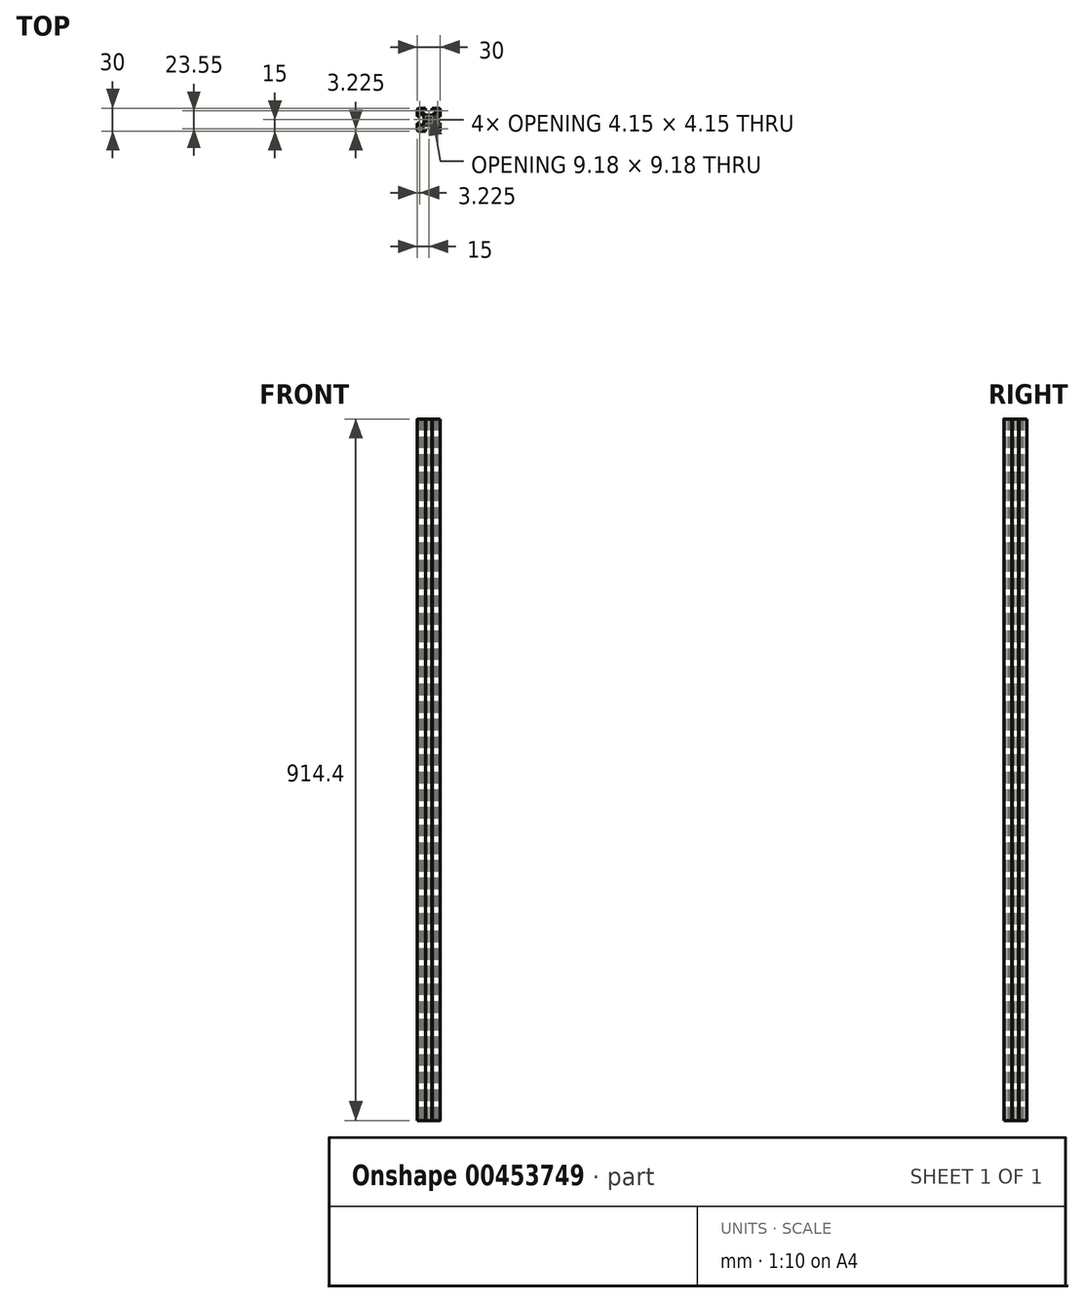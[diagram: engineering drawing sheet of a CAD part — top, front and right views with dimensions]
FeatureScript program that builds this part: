
annotation { "Feature Type Name" : "Feature", "Feature Type Description" : "" }
export const myFeature = defineFeature(function(context is Context, id is Id, definition is map)
    precondition{}
    {
        {
            var Q0;
            Q0=qCreatedBy(makeId("Top.planeOp"),FACE);
            var sketch = newSketch(context, id + "F0", { "sketchPlane" : qUnion([Q0])});
            skLineSegment(sketch, "E0", {"start": v(-12.8, -8.25) * mm, "end": v(-12.8, -4.05) * mm});
            skLineSegment(sketch, "E1", {"start": v(12.8, 4.05) * mm, "end": v(12.8, 8.25) * mm});
            skLineSegment(sketch, "E2", {"start": v(4.6, -3.19) * mm, "end": v(3.27, -1.62) * mm});
            skLineSegment(sketch, "E3", {"start": v(-3.27, 1.62) * mm, "end": v(-4.6, 3.19) * mm});
            skLineSegment(sketch, "E4", {"start": v(8.25, -10.05) * mm, "end": v(4.2, -6) * mm});
            skLineSegment(sketch, "E5", {"start": v(10.05, -8.25) * mm, "end": v(6, -4.2) * mm});
            skLineSegment(sketch, "E6", {"start": v(-3.19, -4.6) * mm, "end": v(-4.6, -3.19) * mm});
            skLineSegment(sketch, "E7", {"start": v(4.6, 3.19) * mm, "end": v(3.19, 4.6) * mm});
            skLineSegment(sketch, "E8", {"start": v(-6, 4.2) * mm, "end": v(-10.05, 8.25) * mm});
            skLineSegment(sketch, "E9", {"start": v(-4.2, 6) * mm, "end": v(-8.25, 10.05) * mm});
            skLineSegment(sketch, "E10", {"start": v(3.19, -4.6) * mm, "end": v(1.62, -3.27) * mm});
            skLineSegment(sketch, "E11", {"start": v(-1.62, 3.27) * mm, "end": v(-3.19, 4.6) * mm});
            skLineSegment(sketch, "E12", {"start": v(-4.05, -12.8) * mm, "end": v(-8.25, -12.8) * mm});
            skLineSegment(sketch, "E13", {"start": v(8.25, 12.8) * mm, "end": v(4.05, 12.8) * mm});
            skLineSegment(sketch, "E14", {"start": v(4.55, -15) * mm, "end": v(13, -15) * mm});
            skLineSegment(sketch, "E15", {"start": v(-13, -15) * mm, "end": v(-4.55, -15) * mm});
            skLineSegment(sketch, "E16", {"start": v(4.05, -14.5) * mm, "end": v(4.55, -14.5) * mm});
            skLineSegment(sketch, "E17", {"start": v(-4.55, -14.5) * mm, "end": v(-4.05, -14.5) * mm});
            skLineSegment(sketch, "E18", {"start": v(9.7, -13.85) * mm, "end": v(12.85, -13.85) * mm});
            skLineSegment(sketch, "E19", {"start": v(-12.85, -13.85) * mm, "end": v(-9.7, -13.85) * mm});
            skLineSegment(sketch, "E20", {"start": v(9.7, -9.7) * mm, "end": v(13.85, -9.7) * mm});
            skLineSegment(sketch, "E21", {"start": v(-13.85, -9.7) * mm, "end": v(-9.7, -9.7) * mm});
            skLineSegment(sketch, "E22", {"start": v(10.05, -8.25) * mm, "end": v(12.8, -8.25) * mm});
            skLineSegment(sketch, "E23", {"start": v(-12.8, -8.25) * mm, "end": v(-10.05, -8.25) * mm});
            skLineSegment(sketch, "E24", {"start": v(-4.2, -6) * mm, "end": v(4.2, -6) * mm});
            skLineSegment(sketch, "E25", {"start": v(14.5, -4.55) * mm, "end": v(15, -4.55) * mm});
            skLineSegment(sketch, "E26", {"start": v(-15, -4.55) * mm, "end": v(-14.5, -4.55) * mm});
            skLineSegment(sketch, "E27", {"start": v(12.8, -4.05) * mm, "end": v(14.5, -4.05) * mm});
            skLineSegment(sketch, "E28", {"start": v(-14.5, -4.05) * mm, "end": v(-12.8, -4.05) * mm});
            skLineSegment(sketch, "E29", {"start": v(-14.5, 4.05) * mm, "end": v(-12.8, 4.05) * mm});
            skLineSegment(sketch, "E30", {"start": v(12.8, 4.05) * mm, "end": v(14.5, 4.05) * mm});
            skLineSegment(sketch, "E31", {"start": v(-15, 4.55) * mm, "end": v(-14.5, 4.55) * mm});
            skLineSegment(sketch, "E32", {"start": v(14.5, 4.55) * mm, "end": v(15, 4.55) * mm});
            skLineSegment(sketch, "E33", {"start": v(-4.2, 6) * mm, "end": v(4.2, 6) * mm});
            skLineSegment(sketch, "E34", {"start": v(-12.8, 8.25) * mm, "end": v(-10.05, 8.25) * mm});
            skLineSegment(sketch, "E35", {"start": v(10.05, 8.25) * mm, "end": v(12.8, 8.25) * mm});
            skLineSegment(sketch, "E36", {"start": v(9.7, 9.7) * mm, "end": v(13.85, 9.7) * mm});
            skLineSegment(sketch, "E37", {"start": v(-13.85, 9.7) * mm, "end": v(-9.7, 9.7) * mm});
            skLineSegment(sketch, "E38", {"start": v(9.7, 13.85) * mm, "end": v(12.85, 13.85) * mm});
            skLineSegment(sketch, "E39", {"start": v(-12.85, 13.85) * mm, "end": v(-9.7, 13.85) * mm});
            skLineSegment(sketch, "E40", {"start": v(-4.55, 14.5) * mm, "end": v(-4.05, 14.5) * mm});
            skLineSegment(sketch, "E41", {"start": v(4.05, 14.5) * mm, "end": v(4.55, 14.5) * mm});
            skLineSegment(sketch, "E42", {"start": v(-13, 15) * mm, "end": v(-4.55, 15) * mm});
            skLineSegment(sketch, "E43", {"start": v(4.55, 15) * mm, "end": v(13, 15) * mm});
            skLineSegment(sketch, "E44", {"start": v(4.05, -12.8) * mm, "end": v(8.25, -12.8) * mm});
            skLineSegment(sketch, "E45", {"start": v(-8.25, 12.8) * mm, "end": v(-4.05, 12.8) * mm});
            skLineSegment(sketch, "E46", {"start": v(-3.19, -4.6) * mm, "end": v(-1.62, -3.27) * mm});
            skLineSegment(sketch, "E47", {"start": v(1.62, 3.27) * mm, "end": v(3.19, 4.6) * mm});
            skLineSegment(sketch, "E48", {"start": v(-8.25, -10.05) * mm, "end": v(-4.2, -6) * mm});
            skLineSegment(sketch, "E49", {"start": v(-10.05, -8.25) * mm, "end": v(-6, -4.2) * mm});
            skLineSegment(sketch, "E50", {"start": v(3.19, -4.6) * mm, "end": v(4.6, -3.19) * mm});
            skLineSegment(sketch, "E51", {"start": v(-4.6, 3.19) * mm, "end": v(-3.19, 4.6) * mm});
            skLineSegment(sketch, "E52", {"start": v(6, 4.2) * mm, "end": v(10.05, 8.25) * mm});
            skLineSegment(sketch, "E53", {"start": v(4.2, 6) * mm, "end": v(8.25, 10.05) * mm});
            skLineSegment(sketch, "E54", {"start": v(-4.6, -3.19) * mm, "end": v(-3.27, -1.62) * mm});
            skLineSegment(sketch, "E55", {"start": v(3.27, 1.62) * mm, "end": v(4.6, 3.19) * mm});
            skLineSegment(sketch, "E56", {"start": v(12.8, -8.25) * mm, "end": v(12.8, -4.05) * mm});
            skLineSegment(sketch, "E57", {"start": v(-12.8, 4.05) * mm, "end": v(-12.8, 8.25) * mm});
            skLineSegment(sketch, "E58", {"start": v(-15, -13) * mm, "end": v(-15, -4.55) * mm});
            skLineSegment(sketch, "E59", {"start": v(-15, 4.55) * mm, "end": v(-15, 13) * mm});
            skLineSegment(sketch, "E60", {"start": v(-14.5, -4.55) * mm, "end": v(-14.5, -4.05) * mm});
            skLineSegment(sketch, "E61", {"start": v(-14.5, 4.05) * mm, "end": v(-14.5, 4.55) * mm});
            skLineSegment(sketch, "E62", {"start": v(-13.85, -12.85) * mm, "end": v(-13.85, -9.7) * mm});
            skLineSegment(sketch, "E63", {"start": v(-13.85, 9.7) * mm, "end": v(-13.85, 12.85) * mm});
            skLineSegment(sketch, "E64", {"start": v(-9.7, -13.85) * mm, "end": v(-9.7, -9.7) * mm});
            skLineSegment(sketch, "E65", {"start": v(-9.7, 9.7) * mm, "end": v(-9.7, 13.85) * mm});
            skLineSegment(sketch, "E66", {"start": v(-8.25, -12.8) * mm, "end": v(-8.25, -10.05) * mm});
            skLineSegment(sketch, "E67", {"start": v(-8.25, 10.05) * mm, "end": v(-8.25, 12.8) * mm});
            skLineSegment(sketch, "E68", {"start": v(-6, -4.2) * mm, "end": v(-6, 4.2) * mm});
            skLineSegment(sketch, "E69", {"start": v(-4.55, -15) * mm, "end": v(-4.55, -14.5) * mm});
            skLineSegment(sketch, "E70", {"start": v(-4.55, 14.5) * mm, "end": v(-4.55, 15) * mm});
            skLineSegment(sketch, "E71", {"start": v(-4.05, -14.5) * mm, "end": v(-4.05, -12.8) * mm});
            skLineSegment(sketch, "E72", {"start": v(-4.05, 12.8) * mm, "end": v(-4.05, 14.5) * mm});
            skLineSegment(sketch, "E73", {"start": v(4.05, -14.5) * mm, "end": v(4.05, -12.8) * mm});
            skLineSegment(sketch, "E74", {"start": v(4.05, 12.8) * mm, "end": v(4.05, 14.5) * mm});
            skLineSegment(sketch, "E75", {"start": v(4.55, -15) * mm, "end": v(4.55, -14.5) * mm});
            skLineSegment(sketch, "E76", {"start": v(4.55, 14.5) * mm, "end": v(4.55, 15) * mm});
            skLineSegment(sketch, "E77", {"start": v(6, -4.2) * mm, "end": v(6, 4.2) * mm});
            skLineSegment(sketch, "E78", {"start": v(8.25, -12.8) * mm, "end": v(8.25, -10.05) * mm});
            skLineSegment(sketch, "E79", {"start": v(8.25, 10.05) * mm, "end": v(8.25, 12.8) * mm});
            skLineSegment(sketch, "E80", {"start": v(9.7, 9.7) * mm, "end": v(9.7, 13.85) * mm});
            skLineSegment(sketch, "E81", {"start": v(9.7, -13.85) * mm, "end": v(9.7, -9.7) * mm});
            skLineSegment(sketch, "E82", {"start": v(13.85, 9.7) * mm, "end": v(13.85, 12.85) * mm});
            skLineSegment(sketch, "E83", {"start": v(13.85, -12.85) * mm, "end": v(13.85, -9.7) * mm});
            skLineSegment(sketch, "E84", {"start": v(14.5, -4.55) * mm, "end": v(14.5, -4.05) * mm});
            skLineSegment(sketch, "E85", {"start": v(14.5, 4.05) * mm, "end": v(14.5, 4.55) * mm});
            skLineSegment(sketch, "E86", {"start": v(15, -13) * mm, "end": v(15, -4.55) * mm});
            skLineSegment(sketch, "E87", {"start": v(15, 4.55) * mm, "end": v(15, 13) * mm});
            skArc(sketch, "E88", {"start": v(-15, -13) * mm, "mid": v(-14.41, -14.41) * mm, "end": v(-13, -15) * mm});
            skArc(sketch, "E89", {"start": v(-13, 15) * mm, "mid": v(-14.41, 14.41) * mm, "end": v(-15, 13) * mm});
            skArc(sketch, "E90", {"start": v(-13.85, -12.85) * mm, "mid": v(-13.56, -13.56) * mm, "end": v(-12.85, -13.85) * mm});
            skArc(sketch, "E91", {"start": v(-12.85, 13.85) * mm, "mid": v(-13.56, 13.56) * mm, "end": v(-13.85, 12.85) * mm});
            skArc(sketch, "E92", {"start": v(-1.62, -3.27) * mm, "mid": v(0, -3.65) * mm, "end": v(1.62, -3.27) * mm});
            skArc(sketch, "E93", {"start": v(-3.27, 1.62) * mm, "mid": v(-3.65, 0) * mm, "end": v(-3.27, -1.62) * mm});
            skArc(sketch, "E94", {"start": v(1.62, 3.27) * mm, "mid": v(0, 3.65) * mm, "end": v(-1.62, 3.27) * mm});
            skArc(sketch, "E95", {"start": v(3.27, -1.62) * mm, "mid": v(3.65, 0) * mm, "end": v(3.27, 1.62) * mm});
            skArc(sketch, "E96", {"start": v(12.85, -13.85) * mm, "mid": v(13.56, -13.56) * mm, "end": v(13.85, -12.85) * mm});
            skArc(sketch, "E97", {"start": v(13.85, 12.85) * mm, "mid": v(13.56, 13.56) * mm, "end": v(12.85, 13.85) * mm});
            skArc(sketch, "E98", {"start": v(13, -15) * mm, "mid": v(14.41, -14.41) * mm, "end": v(15, -13) * mm});
            skArc(sketch, "E99", {"start": v(15, 13) * mm, "mid": v(14.41, 14.41) * mm, "end": v(13, 15) * mm});
            skSolve(sketch);
        }
        {
            var Q0;
            Q0=makeQuery(id+"F0.imprint","IMPRINT",FACE,{"disambiguationData":[TD([[makeQuery(id+"F0.imprint","IMPRINT",EDGE,{"derivedFrom":sQuery(id+"F0.wireOp",EDGE,"E0")}),1.0]])]});
            extrude(context, id + "F1", {"entities" : qUnion([Q0]), "depth" : 914.4 * mm});
        }
    });
